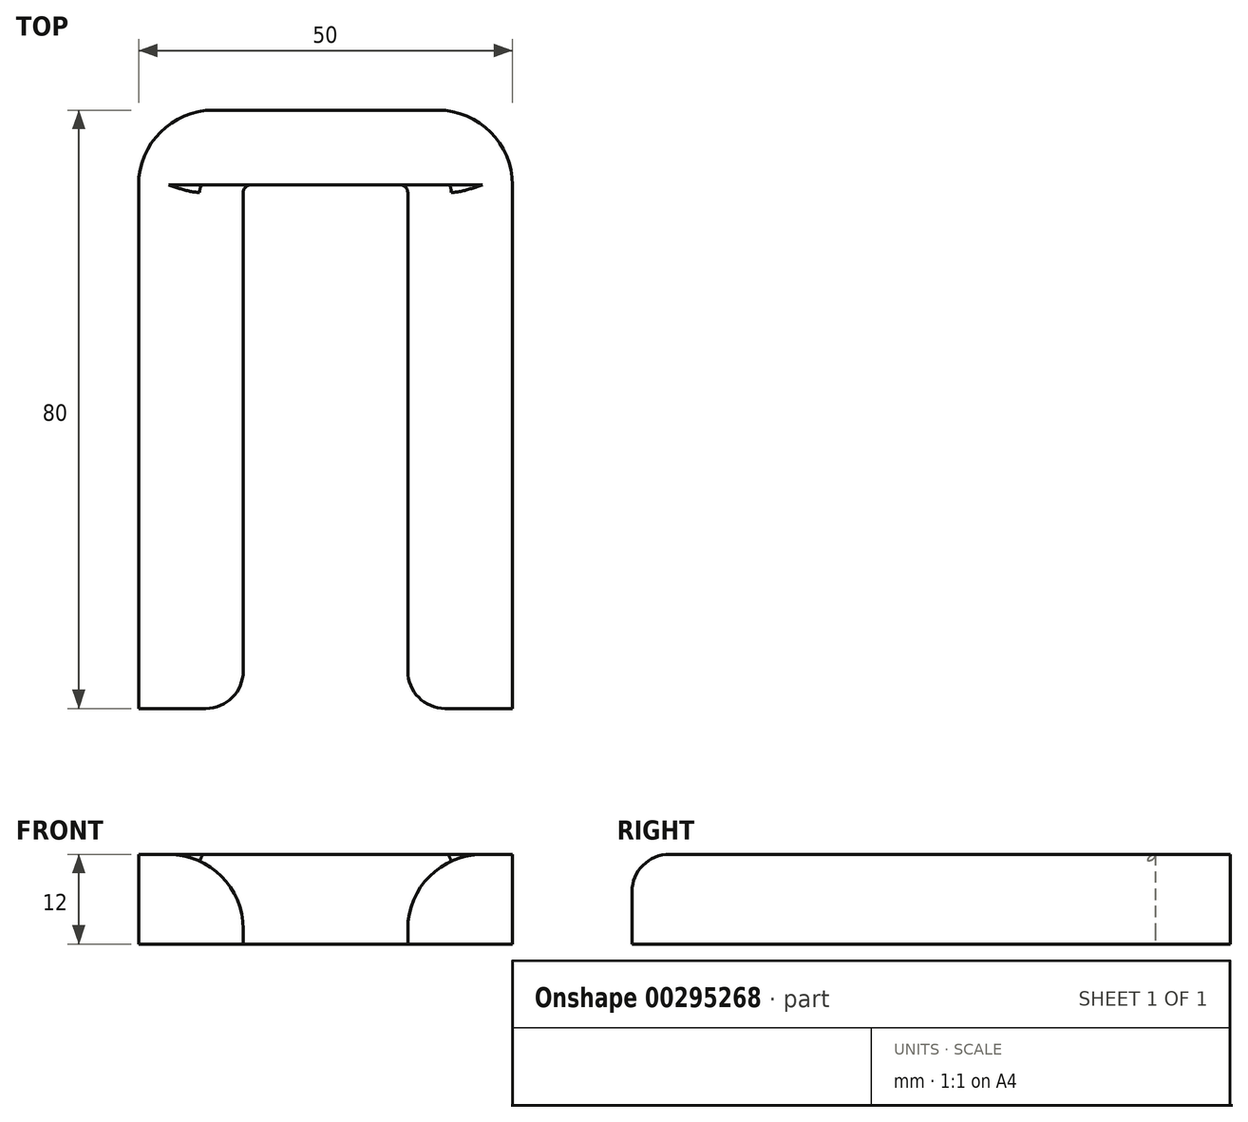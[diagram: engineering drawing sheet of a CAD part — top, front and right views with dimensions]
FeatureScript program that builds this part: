
annotation { "Feature Type Name" : "Feature", "Feature Type Description" : "" }
export const myFeature = defineFeature(function(context is Context, id is Id, definition is map)
    precondition{}
    {
        {
            var Q0;
            Q0=qCreatedBy(makeId("Front.planeOp"),FACE);
            var sketch = newSketch(context, id + "F0", { "sketchPlane" : qUnion([Q0])});
            skLineSegment(sketch, "E0.bottom", {"start": v(0, 0) * mm, "end": v(50, 0) * mm});
            skLineSegment(sketch, "E0.top", {"start": v(0, 12) * mm, "end": v(50, 12) * mm});
            skLineSegment(sketch, "E0.left", {"start": v(0, 0) * mm, "end": v(0, 12) * mm});
            skLineSegment(sketch, "E0.right", {"start": v(50, 0) * mm, "end": v(50, 12) * mm});
            skSolve(sketch);
        }
        {
            var Q0;
            Q0=makeQuery(id+"F0.imprint","IMPRINT",FACE,{"disambiguationData":[TD([[makeQuery(id+"F0.imprint","IMPRINT",EDGE,{"derivedFrom":sQuery(id+"F0.wireOp",EDGE,"E0.bottom")}),1.0]])]});
            extrude(context, id + "F1", {"entities" : qUnion([Q0]), "depth" : 10 * mm});
        }
        {
            var Q0;
            Q0=makeQuery(id+"F1.opExtrude","CAP_FACE",FACE,{"disambiguationData":[OSD([sQuery(id+"F0.wireOp",EDGE,"E0.bottom"),sQuery(id+"F0.wireOp",EDGE,"E0.top"),sQuery(id+"F0.wireOp",EDGE,"E0.left"),sQuery(id+"F0.wireOp",EDGE,"E0.right")])],"isStart":false});
            var sketch = newSketch(context, id + "F2", { "sketchPlane" : qUnion([Q0])});
            skLineSegment(sketch, "E1", {"start": v(25, 12) * mm, "end": v(25, 0) * mm, "construction": true});
            skLineSegment(sketch, "E2.bottom", {"start": v(0, 12) * mm, "end": v(14, 12) * mm});
            skLineSegment(sketch, "E2.top", {"start": v(0, 0) * mm, "end": v(14, 0) * mm});
            skLineSegment(sketch, "E2.left", {"start": v(0, 12) * mm, "end": v(0, 0) * mm});
            skLineSegment(sketch, "E2.right", {"start": v(14, 12) * mm, "end": v(14, 0) * mm});
            skLineSegment(sketch, "E3.MirrorCS", {"start": v(36, 12) * mm, "end": v(36, 0) * mm});
            skLineSegment(sketch, "E4.MirrorCS", {"start": v(50, 12) * mm, "end": v(50, 0) * mm});
            skLineSegment(sketch, "E5.MirrorCS", {"start": v(50, 12) * mm, "end": v(36, 12) * mm});
            skLineSegment(sketch, "E6.MirrorCS", {"start": v(50, 0) * mm, "end": v(36, 0) * mm});
            skSolve(sketch);
        }
        {
            var Q0;
            Q0=makeQuery(id+"F2.imprint","IMPRINT",FACE,{"disambiguationData":[TD([[makeQuery(id+"F2.imprint","IMPRINT",EDGE,{"derivedFrom":sQuery(id+"F2.wireOp",EDGE,"E2.bottom")}),-1.0]])]});
            var Q1;
            Q1=makeQuery(id+"F2.imprint","IMPRINT",FACE,{"disambiguationData":[TD([[makeQuery(id+"F2.imprint","IMPRINT",EDGE,{"derivedFrom":sQuery(id+"F2.wireOp",EDGE,"E3.MirrorCS")}),1.0]])]});
            extrude(context, id + "F3", {"entities" : qUnion([Q0, Q1]), "operationType" : NewBodyOperationType.ADD, "depth" : 70 * mm});
        }
        {
            var Q0;
            Q0=makeQuery(id+"F3.opExtrude","SWEPT_EDGE",EDGE,{"disambiguationData":[OSD([sQuery(id+"F0.wireOp",EDGE,"E0.top"),sQuery(id+"F2.wireOp",EDGE,"E2.bottom"),sQuery(id+"F2.wireOp",EDGE,"E2.right")])]});
            var Q1;
            Q1=makeQuery(id+"F3.opExtrude","SWEPT_EDGE",EDGE,{"disambiguationData":[OSD([sQuery(id+"F0.wireOp",EDGE,"E0.top"),sQuery(id+"F2.wireOp",EDGE,"E3.MirrorCS"),sQuery(id+"F2.wireOp",EDGE,"E5.MirrorCS")])]});
            fillet(context, id + "F4", {"entities" : qUnion([Q0, Q1]), "radius" : 10 * mm, "tangentPropagation" : true, "allowEdgeOverflow" : false});
        }
        {
            var Q0;
            {var subQ0=sQuery(id+"F2.wireOp",EDGE,"E2.right");var subQ1=sQuery(id+"F2.wireOp",EDGE,"E2.bottom");Q0=makeQuery(id+"F4.opFillet","BLEND_EDGE",EDGE,{"blendedFrom":[makeQuery(id+"F3.opExtrude","SWEPT_EDGE",EDGE,{"disambiguationData":[OSD([sQuery(id+"F0.wireOp",EDGE,"E0.top"),subQ1,subQ0])]}),makeQuery(id+"F3.opExtrude","CAP_FACE",FACE,{"disambiguationData":[OSD([subQ1,sQuery(id+"F2.wireOp",EDGE,"E2.top"),sQuery(id+"F2.wireOp",EDGE,"E2.left"),subQ0])],"isStart":false})],"blendedInto":[makeQuery(id+"F3.opExtrude","CAP_FACE",FACE,{"disambiguationData":[OSD([subQ1,sQuery(id+"F2.wireOp",EDGE,"E2.top"),sQuery(id+"F2.wireOp",EDGE,"E2.left"),subQ0])],"isStart":false})]});}
            var Q1;
            {var subQ0=sQuery(id+"F2.wireOp",EDGE,"E5.MirrorCS");var subQ1=sQuery(id+"F2.wireOp",EDGE,"E3.MirrorCS");Q1=makeQuery(id+"F4.opFillet","BLEND_EDGE",EDGE,{"blendedFrom":[makeQuery(id+"F3.opExtrude","SWEPT_EDGE",EDGE,{"disambiguationData":[OSD([sQuery(id+"F0.wireOp",EDGE,"E0.top"),subQ1,subQ0])]}),makeQuery(id+"F3.opExtrude","CAP_FACE",FACE,{"disambiguationData":[OSD([subQ1,sQuery(id+"F2.wireOp",EDGE,"E4.MirrorCS"),subQ0,sQuery(id+"F2.wireOp",EDGE,"E6.MirrorCS")])],"isStart":false})],"blendedInto":[makeQuery(id+"F3.opExtrude","CAP_FACE",FACE,{"disambiguationData":[OSD([subQ1,sQuery(id+"F2.wireOp",EDGE,"E4.MirrorCS"),subQ0,sQuery(id+"F2.wireOp",EDGE,"E6.MirrorCS")])],"isStart":false})]});}
            fillet(context, id + "F5", {"entities" : qUnion([Q0, Q1]), "radius" : 5 * mm, "tangentPropagation" : true, "allowEdgeOverflow" : false});
        }
        {
            var Q0;
            {var subQ0=sQuery(id+"F0.wireOp",EDGE,"E0.top");Q0=makeQuery(id+"F4.opFillet","BLEND_EDGE",EDGE,{"blendedFrom":[makeQuery(id+"F3.opExtrude","SWEPT_EDGE",EDGE,{"disambiguationData":[OSD([subQ0,sQuery(id+"F2.wireOp",EDGE,"E2.bottom"),sQuery(id+"F2.wireOp",EDGE,"E2.right")])]}),makeQuery(id+"F1.opExtrude","CAP_FACE",FACE,{"disambiguationData":[OSD([sQuery(id+"F0.wireOp",EDGE,"E0.bottom"),subQ0,sQuery(id+"F0.wireOp",EDGE,"E0.left"),sQuery(id+"F0.wireOp",EDGE,"E0.right")])],"isStart":false})],"blendedInto":[makeQuery(id+"F1.opExtrude","CAP_FACE",FACE,{"disambiguationData":[OSD([sQuery(id+"F0.wireOp",EDGE,"E0.bottom"),subQ0,sQuery(id+"F0.wireOp",EDGE,"E0.left"),sQuery(id+"F0.wireOp",EDGE,"E0.right")])],"isStart":false})]});}
            var Q1;
            {var subQ0=sQuery(id+"F0.wireOp",EDGE,"E0.top");Q1=makeQuery(id+"F4.opFillet","BLEND_EDGE",EDGE,{"blendedFrom":[makeQuery(id+"F3.opExtrude","SWEPT_EDGE",EDGE,{"disambiguationData":[OSD([subQ0,sQuery(id+"F2.wireOp",EDGE,"E3.MirrorCS"),sQuery(id+"F2.wireOp",EDGE,"E5.MirrorCS")])]}),makeQuery(id+"F1.opExtrude","CAP_FACE",FACE,{"disambiguationData":[OSD([sQuery(id+"F0.wireOp",EDGE,"E0.bottom"),subQ0,sQuery(id+"F0.wireOp",EDGE,"E0.left"),sQuery(id+"F0.wireOp",EDGE,"E0.right")])],"isStart":false})],"blendedInto":[makeQuery(id+"F1.opExtrude","CAP_FACE",FACE,{"disambiguationData":[OSD([sQuery(id+"F0.wireOp",EDGE,"E0.bottom"),subQ0,sQuery(id+"F0.wireOp",EDGE,"E0.left"),sQuery(id+"F0.wireOp",EDGE,"E0.right")])],"isStart":false})]});}
            fillet(context, id + "F6", {"entities" : qUnion([Q0, Q1]), "radius" : 1 * mm, "tangentPropagation" : true, "allowEdgeOverflow" : false});
        }
        {
            var Q0;
            Q0=makeQuery(id+"F1.opExtrude","CAP_EDGE",EDGE,{"disambiguationData":[OSD([sQuery(id+"F0.wireOp",EDGE,"E0.right")])],"isStart":true});
            var Q1;
            Q1=makeQuery(id+"F1.opExtrude","CAP_EDGE",EDGE,{"disambiguationData":[OSD([sQuery(id+"F0.wireOp",EDGE,"E0.left")])],"isStart":true});
            fillet(context, id + "F7", {"entities" : qUnion([Q0, Q1]), "radius" : 10 * mm, "tangentPropagation" : true, "allowEdgeOverflow" : false});
        }
    });
